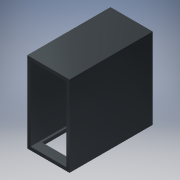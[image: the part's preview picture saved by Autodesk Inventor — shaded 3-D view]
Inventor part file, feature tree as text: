
AUTODESK INVENTOR PART (.ipt)
format: ipt  version: 2018 (Build 220112000, 112)  size: 164,352 bytes
history: native  units: mm
features: extrude x5, sketch x5
ambient origin geometry x8: Origin, YZ Plane, XZ Plane, XY Plane, X Axis, Y Axis, Z Axis, Center Point
bodies: Solid1 (feature_tree)
feature tree (10):
  extrude  "Extrusion1"  Depth=520.0mm
  extrude  "Extrusion2"  Depth=583.0mm TaperAngle=0.0deg
  extrude  "Extrusion3"  Depth=440.0mm
  extrude  "Extrusion4"  Depth=38.0mm
  extrude  "Extrusion5"  Depth=70.0mm
  sketch  "Sketch1"  dims[d0=250.0mm d1=520.0mm]
  sketch  "Sketch2"  dims[d2=23.0mm d3=583.0mm d4=0.0mm]
  sketch  "Sketch3"  dims[d5=220.0mm d6=440.0mm]
  sketch  "Sketch5"  dims[d7=77.0mm d8=38.0mm]
  sketch  "Sketch6"  dims[d9=583.0mm d10=0.0mm d11=70.0mm d12=80.0mm d13=430.0mm d14=143.0mm d15=583.0mm d16=0.0mm d17=47.0mm d18=583.0mm d19=0.0mm d20=16.0mm d21=170.0mm d22=45.0mm d23=16.0mm d24=170.0mm d25=45.0mm d26=10.0mm d27=0.0mm]
